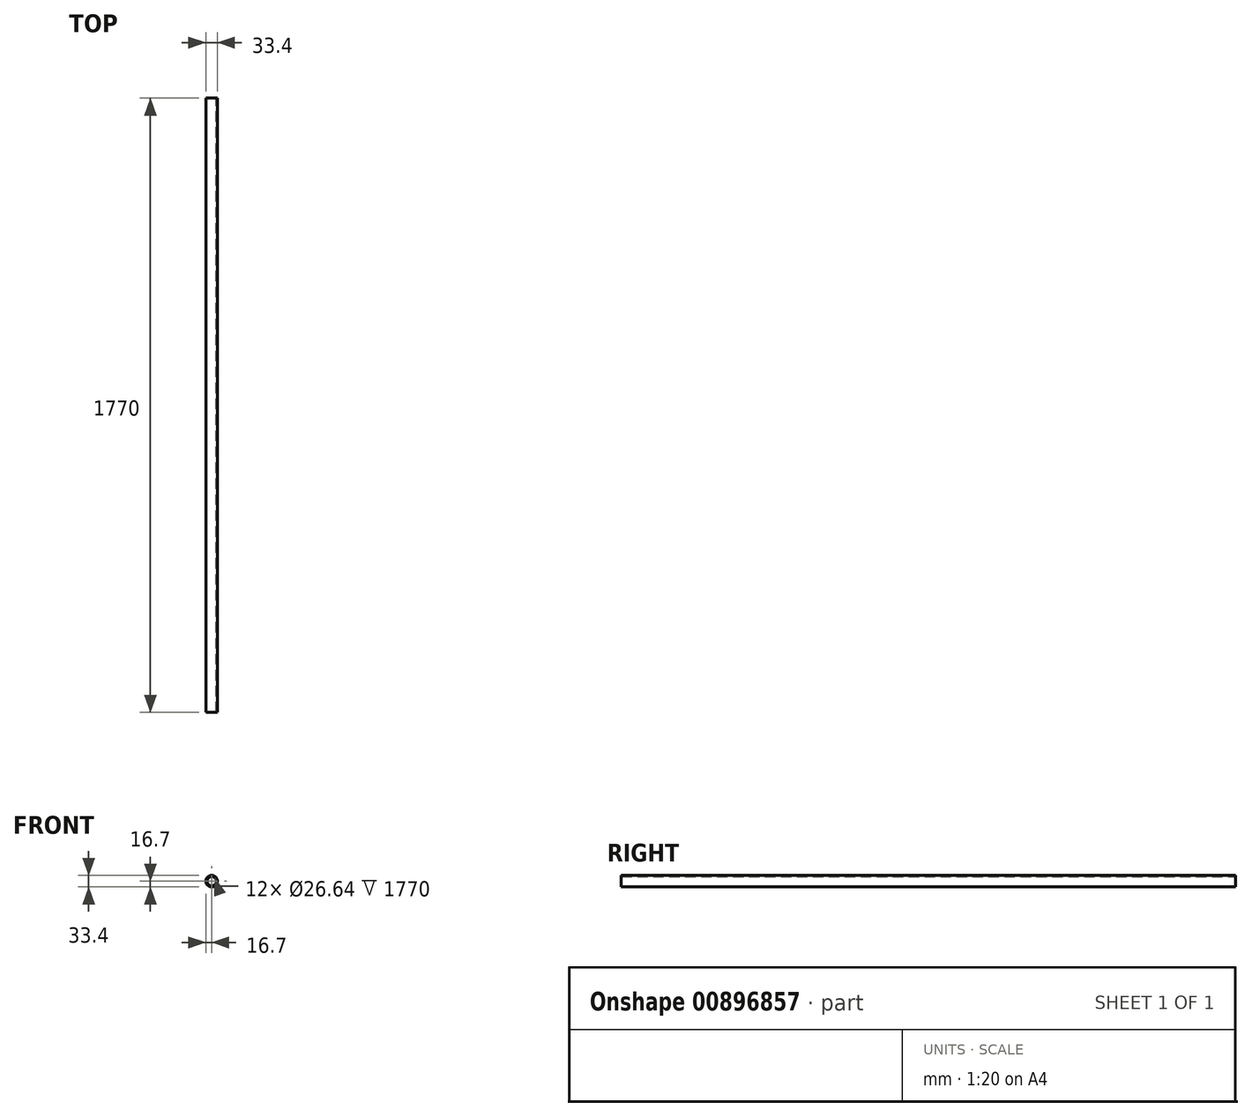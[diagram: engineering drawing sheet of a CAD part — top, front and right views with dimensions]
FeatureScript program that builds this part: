
annotation { "Feature Type Name" : "Feature", "Feature Type Description" : "" }
export const myFeature = defineFeature(function(context is Context, id is Id, definition is map)
    precondition{}
    {
        {
            var Q0;
            Q0=qCreatedBy(makeId("Front.planeOp"),FACE);
            var sketch = newSketch(context, id + "F0", { "sketchPlane" : qUnion([Q0])});
            skCircle(sketch, "E0", {"center": v(0, 0) * mm, "radius": 16.7 * mm});
            skCircle(sketch, "E1", {"center": v(0, 0) * mm, "radius": 13.32 * mm});
            skSolve(sketch);
        }
        {
            var Q0;
            Q0=makeQuery(id+"F0.imprint","IMPRINT",FACE,{"disambiguationData":[TD([[makeQuery(id+"F0.imprint","IMPRINT",EDGE,{"derivedFrom":sQuery(id+"F0.wireOp",EDGE,"E0")}),1.0]])]});
            extrude(context, id + "F1", {"entities" : qUnion([Q0]), "endBound" : BoundingType.SYMMETRIC, "depth" : 1770 * mm, "offsetDistance" : 25.4 * mm});
        }
    });
